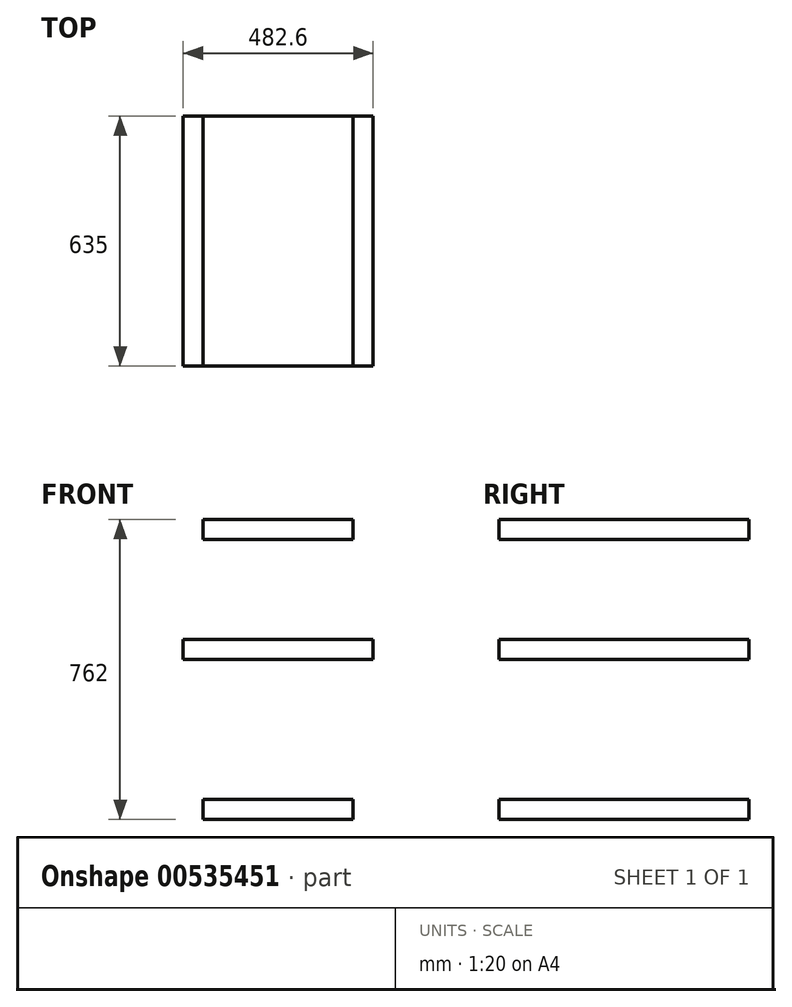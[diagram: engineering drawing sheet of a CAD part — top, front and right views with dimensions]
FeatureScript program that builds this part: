
annotation { "Feature Type Name" : "Feature", "Feature Type Description" : "" }
export const myFeature = defineFeature(function(context is Context, id is Id, definition is map)
    precondition{}
    {
        {
            var Q0;
            Q0=qCreatedBy(makeId("Front.planeOp"),FACE);
            var sketch = newSketch(context, id + "F0", { "sketchPlane" : qUnion([Q0])});
            skLineSegment(sketch, "E0.bottom", {"start": v(-241.3, 381) * mm, "end": v(241.3, 381) * mm});
            skLineSegment(sketch, "E0.top", {"start": v(-241.3, -381) * mm, "end": v(241.3, -381) * mm});
            skLineSegment(sketch, "E0.left", {"start": v(-241.3, 381) * mm, "end": v(-241.3, -381) * mm});
            skLineSegment(sketch, "E0.right", {"start": v(241.3, 381) * mm, "end": v(241.3, -381) * mm});
            skPoint(sketch, "E0.middle", {"position": v(0, 0) * mm});
            skLineSegment(sketch, "E1", {"start": v(-190.5, 381) * mm, "end": v(-190.5, -381) * mm});
            skLineSegment(sketch, "E2", {"start": v(190.5, 381) * mm, "end": v(190.5, -381) * mm});
            skLineSegment(sketch, "E3", {"start": v(-190.5, -330.2) * mm, "end": v(190.5, -330.2) * mm});
            skLineSegment(sketch, "E4", {"start": v(-190.5, 330.2) * mm, "end": v(190.5, 330.2) * mm});
            skLineSegment(sketch, "E5.bottom", {"start": v(-241.3, 76.2) * mm, "end": v(241.3, 76.2) * mm});
            skLineSegment(sketch, "E5.top", {"start": v(-241.3, 25.4) * mm, "end": v(241.3, 25.4) * mm});
            skLineSegment(sketch, "E5.left", {"start": v(-241.3, 76.2) * mm, "end": v(-241.3, 25.4) * mm});
            skLineSegment(sketch, "E5.right", {"start": v(241.3, 76.2) * mm, "end": v(241.3, 25.4) * mm});
            skSolve(sketch);
        }
        {
            var Q0;
            {var subQ5=sQuery(id+"F0.wireOp",EDGE,"E4");Q0=makeQuery(id+"F0.imprint","IMPRINT",FACE,{"disambiguationData":[TD([[makeQuery(id+"F0.imprint","IMPRINT",EDGE,{"derivedFrom":subQ5}),1.0]])]});}
            var Q1;
            {var subQ4=sQuery(id+"F0.wireOp",EDGE,"E0.right");Q1=makeQuery(id+"F0.imprint","IMPRINT",FACE,{"disambiguationData":[TD([[makeQuery(id+"F0.imprint","IMPRINT",EDGE,{"derivedFrom":subQ4}),-1.0]])]});}
            var Q2;
            {var subQ5=sQuery(id+"F0.wireOp",EDGE,"E3");Q2=makeQuery(id+"F0.imprint","IMPRINT",FACE,{"disambiguationData":[TD([[makeQuery(id+"F0.imprint","IMPRINT",EDGE,{"derivedFrom":subQ5}),-1.0]])]});}
            var Q3;
            {var subQ0=sQuery(id+"F0.wireOp",EDGE,"E0.left");Q3=makeQuery(id+"F0.imprint","IMPRINT",FACE,{"disambiguationData":[TD([[makeQuery(id+"F0.imprint","IMPRINT",EDGE,{"derivedFrom":subQ0}),1.0]])]});}
            var Q4;
            {var subQ0=sQuery(id+"F0.wireOp",EDGE,"E5.bottom");var subQ1=sQuery(id+"F0.wireOp",EDGE,"E1");var subQ2=makeQuery(id+"F0.imprint","INTERSECT",VERTEX,{"derivedFrom":[subQ1,subQ0]});Q4=makeQuery(id+"F0.imprint","IMPRINT",FACE,{"disambiguationData":[TD([[makeQuery(id+"F0.imprint","IMPRINT",EDGE,{"disambiguationData":[TD([[subQ2,-1.0]])],"derivedFrom":subQ1}),1.0]])]});}
            var Q5;
            {var subQ5=sQuery(id+"F0.wireOp",EDGE,"E5.left");Q5=makeQuery(id+"F0.imprint","IMPRINT",FACE,{"disambiguationData":[TD([[makeQuery(id+"F0.imprint","IMPRINT",EDGE,{"derivedFrom":subQ5}),1.0]])]});}
            var Q6;
            {var subQ5=sQuery(id+"F0.wireOp",EDGE,"E5.right");Q6=makeQuery(id+"F0.imprint","IMPRINT",FACE,{"disambiguationData":[TD([[makeQuery(id+"F0.imprint","IMPRINT",EDGE,{"derivedFrom":subQ5}),-1.0]])]});}
            extrude(context, id + "F1", {"entities" : qUnion([Q0, Q1, Q2, Q3, Q4, Q5, Q6]), "oppositeDirection" : true, "depth" : 635 * mm, "offsetDistance" : 25.4 * mm});
        }
        {
            var Q0;
            Q0=makeQuery(id+"F1.opExtrude","SWEPT_FACE",FACE,{"disambiguationData":[OSD([sQuery(id+"F0.wireOp",EDGE,"E0.right")])]});
            var sketch = newSketch(context, id + "F2", { "sketchPlane" : qUnion([Q0])});
            skLineSegment(sketch, "E6.bottom", {"start": v(55.1, 330.2) * mm, "end": v(588.5, 330.2) * mm});
            skLineSegment(sketch, "E6.top", {"start": v(55.1, -330.2) * mm, "end": v(588.5, -330.2) * mm});
            skLineSegment(sketch, "E6.left", {"start": v(55.1, 330.2) * mm, "end": v(55.1, -330.2) * mm});
            skLineSegment(sketch, "E6.right", {"start": v(588.5, 330.2) * mm, "end": v(588.5, -330.2) * mm});
            skLineSegment(sketch, "E7.bottom", {"start": v(0, 76.2) * mm, "end": v(635, 76.2) * mm});
            skLineSegment(sketch, "E7.top", {"start": v(0, 25.4) * mm, "end": v(635, 25.4) * mm});
            skLineSegment(sketch, "E7.left", {"start": v(0, 76.2) * mm, "end": v(0, 25.4) * mm});
            skLineSegment(sketch, "E7.right", {"start": v(635, 76.2) * mm, "end": v(635, 25.4) * mm});
            skSolve(sketch);
        }
        {
            var Q0;
            Q0=makeQuery(id+"F2.imprint","IMPRINT",FACE,{"disambiguationData":[TD([[makeQuery(id+"F2.imprint","IMPRINT",EDGE,{"derivedFrom":sQuery(id+"F2.wireOp",EDGE,"E6.bottom")}),-1.0]])]});
            var Q1;
            {var subQ0=sQuery(id+"F2.wireOp",EDGE,"E6.top");Q1=makeQuery(id+"F2.imprint","IMPRINT",FACE,{"disambiguationData":[TD([[makeQuery(id+"F2.imprint","IMPRINT",EDGE,{"derivedFrom":subQ0}),1.0]])]});}
            extrude(context, id + "F3", {"entities" : qUnion([Q0, Q1]), "operationType" : NewBodyOperationType.REMOVE, "endBound" : BoundingType.THROUGH_ALL, "oppositeDirection" : true, "depth" : 50.8 * mm, "offsetDistance" : 25.4 * mm});
        }
    });
